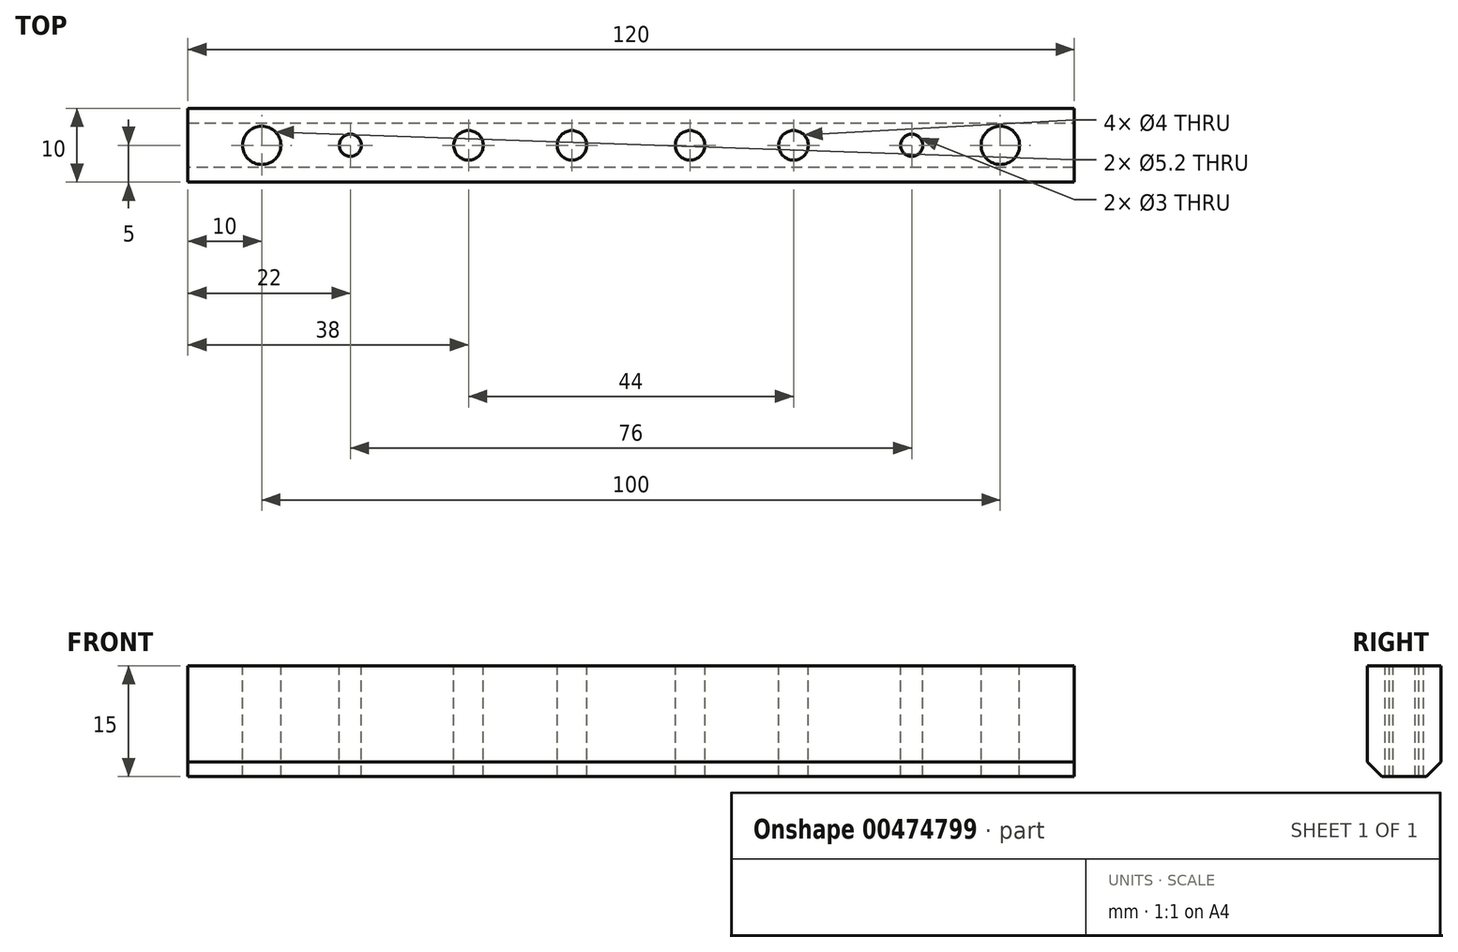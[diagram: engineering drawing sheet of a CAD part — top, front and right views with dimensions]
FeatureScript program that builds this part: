
annotation { "Feature Type Name" : "Feature", "Feature Type Description" : "" }
export const myFeature = defineFeature(function(context is Context, id is Id, definition is map)
    precondition{}
    {
        {
            var Q0;
            Q0=qCreatedBy(makeId("Top.planeOp"),FACE);
            var sketch = newSketch(context, id + "F0", { "sketchPlane" : qUnion([Q0])});
            skLineSegment(sketch, "E0.bottom", {"start": v(60, -5) * mm, "end": v(-60, -5) * mm});
            skLineSegment(sketch, "E0.top", {"start": v(60, 5) * mm, "end": v(-60, 5) * mm});
            skLineSegment(sketch, "E0.left", {"start": v(60, -5) * mm, "end": v(60, 5) * mm});
            skLineSegment(sketch, "E0.right", {"start": v(-60, -5) * mm, "end": v(-60, 5) * mm});
            skPoint(sketch, "E0.middle", {"position": v(0, 0) * mm});
            skCircle(sketch, "E1", {"center": v(-50, 0) * mm, "radius": 2.6 * mm});
            skCircle(sketch, "E2.MirrorC", {"center": v(50, 0) * mm, "radius": 2.6 * mm});
            skCircle(sketch, "E3", {"center": v(-38, 0) * mm, "radius": 1.5 * mm});
            skCircle(sketch, "E4.MirrorC", {"center": v(38, 0) * mm, "radius": 1.5 * mm});
            skCircle(sketch, "E5", {"center": v(-8, 0) * mm, "radius": 2 * mm});
            skCircle(sketch, "E6", {"center": v(-22, 0) * mm, "radius": 2 * mm});
            skCircle(sketch, "E7.MirrorC", {"center": v(8, 0) * mm, "radius": 2 * mm});
            skCircle(sketch, "E8.MirrorC", {"center": v(22, 0) * mm, "radius": 2 * mm});
            skSolve(sketch);
        }
        {
            var Q0;
            Q0 = qSketchRegion(id + "F0", true);
            extrude(context, id + "F1", {"entities" : qUnion([Q0]), "oppositeDirection" : true, "depth" : 15 * mm});
        }
        {
            var Q0;
            Q0=makeQuery(id+"F1.opExtrude","CAP_EDGE",EDGE,{"disambiguationData":[OSD([sQuery(id+"F0.wireOp",EDGE,"E0.bottom")])],"isStart":false});
            var Q1;
            Q1=makeQuery(id+"F1.opExtrude","CAP_EDGE",EDGE,{"disambiguationData":[OSD([sQuery(id+"F0.wireOp",EDGE,"E0.top")])],"isStart":false});
            chamfer(context, id + "F2", {"entities" : qUnion([Q0, Q1]), "width" : 2 * mm, "tangentPropagation" : true});
        }
    });
